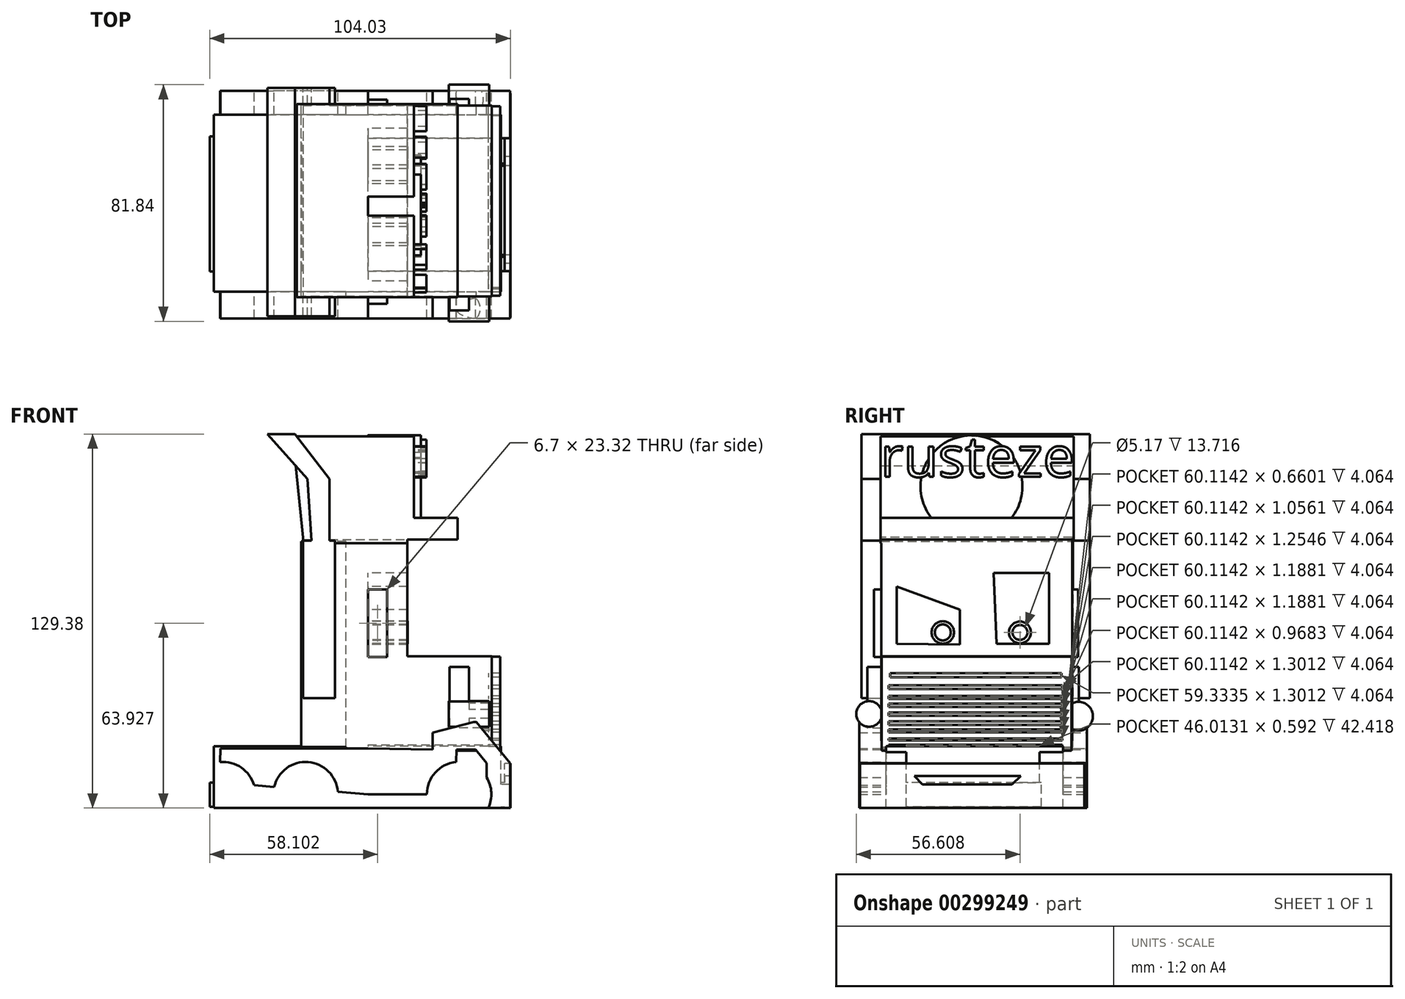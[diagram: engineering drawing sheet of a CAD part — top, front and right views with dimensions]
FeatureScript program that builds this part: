
annotation { "Feature Type Name" : "Feature", "Feature Type Description" : "" }
export const myFeature = defineFeature(function(context is Context, id is Id, definition is map)
    precondition{}
    {
        {
            var Q0;
            Q0=qCreatedBy(makeId("Front.planeOp"),FACE);
            var sketch = newSketch(context, id + "F0", { "sketchPlane" : qUnion([Q0])});
            skLineSegment(sketch, "E0", {"start": v(30.31, -25.21) * mm, "end": v(22.44, -25.21) * mm});
            skLineSegment(sketch, "E1", {"start": v(22.44, -25.21) * mm, "end": v(22.44, -3.93) * mm});
            skLineSegment(sketch, "E2", {"start": v(22.44, -3.93) * mm, "end": v(37.3, 0) * mm});
            skLineSegment(sketch, "E3", {"start": v(37.3, 0) * mm, "end": v(49.26, -14.43) * mm});
            skLineSegment(sketch, "E4", {"start": v(49.26, -14.43) * mm, "end": v(49.26, -39.2) * mm});
            skLineSegment(sketch, "E5", {"start": v(49.26, -39.2) * mm, "end": v(41.1, -34.54) * mm});
            skLineSegment(sketch, "E6", {"start": v(41.1, -34.54) * mm, "end": v(41.1, -14.43) * mm});
            skLineSegment(sketch, "E7", {"start": v(41.1, -14.43) * mm, "end": v(37.3, -9.76) * mm});
            skLineSegment(sketch, "E8", {"start": v(37.3, -9.76) * mm, "end": v(30.6, -9.76) * mm});
            skLineSegment(sketch, "E9", {"start": v(30.6, -9.76) * mm, "end": v(30.31, -25.21) * mm});
            skLineSegment(sketch, "E10", {"start": v(22.44, -9.76) * mm, "end": v(0, -9.34) * mm});
            skLineSegment(sketch, "E11", {"start": v(0, -9.34) * mm, "end": v(0, -25.21) * mm});
            skLineSegment(sketch, "E12", {"start": v(0, -25.21) * mm, "end": v(22.44, -25.21) * mm});
            skLineSegment(sketch, "E13", {"start": v(0, -9.34) * mm, "end": v(-51, -9.34) * mm});
            skLineSegment(sketch, "E14", {"start": v(-51, -9.34) * mm, "end": v(-51.23, -21.17) * mm});
            skLineSegment(sketch, "E15", {"start": v(-51.23, -21.17) * mm, "end": v(0, -25.21) * mm});
            skSolve(sketch);
        }
        {
            var Q0;
            Q0 = qSketchRegion(id + "F0", true);
            extrude(context, id + "F1", {"entities" : qUnion([Q0]), "depth" : 38.86 * mm, "hasSecondDirection" : true, "secondDirectionOppositeDirection" : true, "secondDirectionDepth" : 39.88 * mm});
        }
        {
            var Q0;
            Q0=qCreatedBy(makeId("Front.planeOp"),FACE);
            var sketch = newSketch(context, id + "F2", { "sketchPlane" : qUnion([Q0])});
            skLineSegment(sketch, "E16.bottom", {"start": v(22.74, -10.06) * mm, "end": v(42.85, -10.06) * mm});
            skLineSegment(sketch, "E16.top", {"start": v(22.74, 22.59) * mm, "end": v(42.85, 22.59) * mm});
            skLineSegment(sketch, "E16.left", {"start": v(22.74, -10.06) * mm, "end": v(22.74, 22.59) * mm});
            skLineSegment(sketch, "E16.right", {"start": v(42.85, -10.06) * mm, "end": v(42.85, 22.59) * mm});
            skLineSegment(sketch, "E17.bottom", {"start": v(22.74, -10.06) * mm, "end": v(0, -10.06) * mm});
            skLineSegment(sketch, "E17.top", {"start": v(22.74, 22.59) * mm, "end": v(0, 22.59) * mm});
            skLineSegment(sketch, "E17.right", {"start": v(0, -10.06) * mm, "end": v(0, 22.59) * mm});
            skLineSegment(sketch, "E18.bottom", {"start": v(0, -10.06) * mm, "end": v(-7.58, -10.06) * mm});
            skLineSegment(sketch, "E18.top", {"start": v(0, 22.59) * mm, "end": v(-7.58, 22.59) * mm});
            skLineSegment(sketch, "E18.right", {"start": v(-7.58, -10.06) * mm, "end": v(-7.58, 22.59) * mm});
            skLineSegment(sketch, "E19.bottom", {"start": v(-7.58, 22.59) * mm, "end": v(13.7, 22.59) * mm});
            skLineSegment(sketch, "E19.top", {"start": v(-7.58, 61.65) * mm, "end": v(13.7, 61.65) * mm});
            skLineSegment(sketch, "E19.left", {"start": v(-7.58, 22.59) * mm, "end": v(-7.58, 61.65) * mm});
            skLineSegment(sketch, "E19.right", {"start": v(13.7, 22.59) * mm, "end": v(13.7, 61.65) * mm});
            skSolve(sketch);
        }
        {
            var Q0;
            Q0 = qSketchRegion(id + "F2", true);
            extrude(context, id + "F3", {"entities" : qUnion([Q0]), "operationType" : NewBodyOperationType.ADD, "depth" : 31.24 * mm, "hasSecondDirection" : true, "secondDirectionOppositeDirection" : true, "secondDirectionDepth" : 34.8 * mm});
        }
        {
            var Q0;
            Q0=qCreatedBy(makeId("Front.planeOp"),FACE);
            var sketch = newSketch(context, id + "F4", { "sketchPlane" : qUnion([Q0])});
            skLineSegment(sketch, "E20.bottom", {"start": v(28.27, -2.77) * mm, "end": v(34.98, -2.77) * mm});
            skLineSegment(sketch, "E20.top", {"start": v(28.27, 18.8) * mm, "end": v(34.98, 18.8) * mm});
            skLineSegment(sketch, "E20.left", {"start": v(28.27, -2.77) * mm, "end": v(28.27, 18.8) * mm});
            skLineSegment(sketch, "E20.right", {"start": v(34.98, -2.77) * mm, "end": v(34.98, 18.8) * mm});
            skSolve(sketch);
        }
        {
            var Q0;
            Q0 = qSketchRegion(id + "F4", true);
            extrude(context, id + "F5", {"entities" : qUnion([Q0]), "operationType" : NewBodyOperationType.ADD, "depth" : 36.07 * mm, "hasSecondDirection" : true, "secondDirectionOppositeDirection" : true, "secondDirectionDepth" : 37.08 * mm});
        }
        {
            var Q0;
            Q0=qCreatedBy(makeId("Front.planeOp"),FACE);
            var sketch = newSketch(context, id + "F6", { "sketchPlane" : qUnion([Q0])});
            skLineSegment(sketch, "E21.bottom", {"start": v(0, 45.62) * mm, "end": v(6.7, 45.62) * mm});
            skLineSegment(sketch, "E21.top", {"start": v(0, 22.3) * mm, "end": v(6.7, 22.3) * mm});
            skLineSegment(sketch, "E21.left", {"start": v(0, 45.62) * mm, "end": v(0, 22.3) * mm});
            skLineSegment(sketch, "E21.right", {"start": v(6.7, 45.62) * mm, "end": v(6.7, 22.3) * mm});
            skSolve(sketch);
        }
        {
            var Q0;
            Q0 = qSketchRegion(id + "F6", true);
            extrude(context, id + "F7", {"entities" : qUnion([Q0]), "operationType" : NewBodyOperationType.ADD, "depth" : 33.78 * mm, "hasSecondDirection" : true, "secondDirectionOppositeDirection" : true, "secondDirectionDepth" : 36.83 * mm});
        }
        {
            var Q0;
            Q0=qCreatedBy(makeId("Front.planeOp"),FACE);
            var sketch = newSketch(context, id + "F8", { "sketchPlane" : qUnion([Q0])});
            skLineSegment(sketch, "E22.bottom", {"start": v(-7.58, -8.9) * mm, "end": v(-23.03, -8.9) * mm});
            skLineSegment(sketch, "E22.top", {"start": v(-7.58, 14.72) * mm, "end": v(-23.03, 14.72) * mm});
            skLineSegment(sketch, "E22.left", {"start": v(-7.58, -8.9) * mm, "end": v(-7.58, 14.72) * mm});
            skLineSegment(sketch, "E22.right", {"start": v(-23.03, -8.9) * mm, "end": v(-23.03, 14.72) * mm});
            skLineSegment(sketch, "E23.top", {"start": v(-7.58, 62.23) * mm, "end": v(-23.03, 62.23) * mm});
            skLineSegment(sketch, "E23.left", {"start": v(-7.58, 14.72) * mm, "end": v(-7.58, 62.23) * mm});
            skLineSegment(sketch, "E23.right", {"start": v(-23.03, 14.72) * mm, "end": v(-23.03, 62.23) * mm});
            skSolve(sketch);
        }
        {
            var Q0;
            Q0 = qSketchRegion(id + "F8", true);
            extrude(context, id + "F9", {"entities" : qUnion([Q0]), "operationType" : NewBodyOperationType.ADD, "depth" : 31.24 * mm, "hasSecondDirection" : true, "secondDirectionOppositeDirection" : true, "secondDirectionDepth" : 35.05 * mm});
        }
        {
            var Q0;
            Q0=qCreatedBy(makeId("Front.planeOp"),FACE);
            var sketch = newSketch(context, id + "F10", { "sketchPlane" : qUnion([Q0])});
            skLineSegment(sketch, "E24", {"start": v(-19.53, 8.02) * mm, "end": v(-11.37, 8.02) * mm});
            skLineSegment(sketch, "E25", {"start": v(-11.37, 8.02) * mm, "end": v(-11.37, 62.52) * mm});
            skLineSegment(sketch, "E26", {"start": v(-11.37, 62.52) * mm, "end": v(-22.44, 62.52) * mm});
            skLineSegment(sketch, "E27", {"start": v(-22.44, 62.52) * mm, "end": v(-22.44, 8.02) * mm});
            skLineSegment(sketch, "E28", {"start": v(-19.53, 8.02) * mm, "end": v(-22.44, 8.02) * mm});
            skLineSegment(sketch, "E29", {"start": v(-13.34, 62.52) * mm, "end": v(-13.34, 83.86) * mm});
            skLineSegment(sketch, "E30", {"start": v(-13.34, 83.86) * mm, "end": v(-25.2, 99.4) * mm});
            skLineSegment(sketch, "E31", {"start": v(-25.2, 99.4) * mm, "end": v(-34.7, 99.4) * mm});
            skLineSegment(sketch, "E32", {"start": v(-34.7, 99.4) * mm, "end": v(-20.93, 83.86) * mm});
            skLineSegment(sketch, "E33", {"start": v(-20.93, 83.86) * mm, "end": v(-19.53, 62.52) * mm});
            skLineSegment(sketch, "E34", {"start": v(-19.53, 62.52) * mm, "end": v(-13.34, 62.52) * mm});
            skSolve(sketch);
        }
        {
            var Q0;
            Q0 = qSketchRegion(id + "F10", true);
            extrude(context, id + "F11", {"entities" : qUnion([Q0]), "operationType" : NewBodyOperationType.ADD, "depth" : 38.1 * mm, "hasSecondDirection" : true, "secondDirectionOppositeDirection" : true, "secondDirectionDepth" : 40.9 * mm});
        }
        {
            var Q0;
            Q0=qCreatedBy(makeId("Front.planeOp"),FACE);
            var sketch = newSketch(context, id + "F12", { "sketchPlane" : qUnion([Q0])});
            skLineSegment(sketch, "E35", {"start": v(-22.36, 62.88) * mm, "end": v(31.04, 62.88) * mm});
            skLineSegment(sketch, "E36", {"start": v(31.04, 62.88) * mm, "end": v(31.04, 70.4) * mm});
            skLineSegment(sketch, "E37", {"start": v(31.04, 70.4) * mm, "end": v(15.99, 70.4) * mm});
            skLineSegment(sketch, "E38", {"start": v(15.99, 70.4) * mm, "end": v(15.99, 98.62) * mm});
            skLineSegment(sketch, "E39", {"start": v(15.99, 98.62) * mm, "end": v(-26.03, 98.62) * mm});
            skLineSegment(sketch, "E40", {"start": v(-26.03, 98.62) * mm, "end": v(-22.36, 62.88) * mm});
            skSolve(sketch);
        }
        {
            var Q0;
            Q0 = qSketchRegion(id + "F12", true);
            extrude(context, id + "F13", {"entities" : qUnion([Q0]), "operationType" : NewBodyOperationType.ADD, "depth" : 31.5 * mm, "hasSecondDirection" : true, "secondDirectionOppositeDirection" : true, "secondDirectionDepth" : 35.3 * mm});
        }
        {
            var Q0;
            Q0=qCreatedBy(makeId("Right.planeOp"),FACE);
            var sketch = newSketch(context, id + "F14", { "sketchPlane" : qUnion([Q0])});
            skLineSegment(sketch, "E41.bottom", {"start": v(23.51, -8.04) * mm, "end": v(-22.5, -8.04) * mm});
            skLineSegment(sketch, "E41.top", {"start": v(23.51, -39.28) * mm, "end": v(-22.5, -39.28) * mm});
            skLineSegment(sketch, "E41.left", {"start": v(23.51, -8.04) * mm, "end": v(23.51, -39.28) * mm});
            skLineSegment(sketch, "E41.right", {"start": v(-22.5, -8.04) * mm, "end": v(-22.5, -39.28) * mm});
            skSolve(sketch);
        }
        {
            var Q0;
            Q0 = qSketchRegion(id + "F14", true);
            extrude(context, id + "F15", {"entities" : qUnion([Q0]), "operationType" : NewBodyOperationType.REMOVE, "oppositeDirection" : true, "depth" : 104.9 * mm, "hasSecondDirection" : true, "secondDirectionOppositeDirection" : false, "secondDirectionDepth" : 66.3 * mm});
        }
        {
            var Q0;
            Q0=qCreatedBy(makeId("Front.planeOp"),FACE);
            var sketch = newSketch(context, id + "F16", { "sketchPlane" : qUnion([Q0])});
            skCircle(sketch, "E42", {"center": v(-50.09, -25.17) * mm, "radius": 11.16 * mm});
            skCircle(sketch, "E43", {"center": v(-21.54, -25.17) * mm, "radius": 11.16 * mm});
            skCircle(sketch, "E44", {"center": v(31.55, -25.17) * mm, "radius": 11.16 * mm});
            skSolve(sketch);
        }
        {
            var Q0;
            Q0 = qSketchRegion(id + "F16", true);
            extrude(context, id + "F17", {"entities" : qUnion([Q0]), "operationType" : NewBodyOperationType.REMOVE, "depth" : 52.58 * mm, "hasSecondDirection" : true, "secondDirectionOppositeDirection" : true, "secondDirectionDepth" : 51.3 * mm});
        }
        {
            var Q0;
            Q0=qCreatedBy(makeId("Front.planeOp"),FACE);
            var sketch = newSketch(context, id + "F18", { "sketchPlane" : qUnion([Q0])});
            skCircle(sketch, "E45", {"center": v(31.68, -25.5) * mm, "radius": 9.95 * mm, "construction": true});
            skCircle(sketch, "E46", {"center": v(31.68, -25.5) * mm, "radius": 3.81 * mm});
            skLineSegment(sketch, "E47", {"start": v(31.68, -25.5) * mm, "end": v(-56.9, -25.5) * mm, "construction": true});
            skCircle(sketch, "E48", {"center": v(-21.2, -25.5) * mm, "radius": 3.81 * mm});
            skCircle(sketch, "E49", {"center": v(-49.48, -25.5) * mm, "radius": 3.81 * mm});
            skSolve(sketch);
        }
        {
            var Q0;
            Q0 = qSketchRegion(id + "F18", true);
            extrude(context, id + "F19", {"entities" : qUnion([Q0]), "operationType" : NewBodyOperationType.REMOVE, "depth" : 49.02 * mm, "hasSecondDirection" : true, "secondDirectionOppositeDirection" : true, "secondDirectionDepth" : 51.56 * mm});
        }
        {
            var Q0;
            Q0 = qSketchRegion(id + "F18", true);
            extrude(context, id + "F20", {"entities" : qUnion([Q0]), "depth" : 25.4 * mm});
        }
        {
            var Q0;
            Q0=makeQuery(id+"F13.opExtrude","SWEPT_FACE",FACE,{"disambiguationData":[OSD([sQuery(id+"F12.wireOp",EDGE,"E38")])]});
            var sketch = newSketch(context, id + "F21", { "sketchPlane" : qUnion([Q0])});
            skText(sketch, "E50", { "text": "rusteze", "fontName": "OpenSans-Regular.ttf"});
            const initialGuessF21  = {"E50": [-0.0315, 0.08457, 1, 0, 0.01406]};
            skSetInitialGuess(sketch, initialGuessF21);
            skSolve(sketch);
        }
        {
            var Q0;
            Q0 = qSketchRegion(id + "F21", true);
            extrude(context, id + "F22", {"entities" : qUnion([Q0]), "operationType" : NewBodyOperationType.ADD, "depth" : 4.32 * mm});
        }
        {
            var Q0;
            Q0=qCreatedBy(makeId("Right.planeOp"),FACE);
            var sketch = newSketch(context, id + "F23", { "sketchPlane" : qUnion([Q0])});
            skCircle(sketch, "E51", {"center": v(0, 81.3) * mm, "radius": 17.63 * mm});
            skSolve(sketch);
        }
        {
            var Q0;
            Q0 = qSketchRegion(id + "F23", true);
            extrude(context, id + "F24", {"entities" : qUnion([Q0]), "operationType" : NewBodyOperationType.ADD, "depth" : 18.29 * mm});
        }
        {
            var Q0;
            Q0=qCreatedBy(makeId("Right.planeOp"),FACE);
            var sketch = newSketch(context, id + "F25", { "sketchPlane" : qUnion([Q0])});
            skLineSegment(sketch, "E52", {"start": v(-25.86, 26.89) * mm, "end": v(-25.86, 46.7) * mm});
            skLineSegment(sketch, "E53", {"start": v(-25.86, 46.7) * mm, "end": v(-4.03, 38.64) * mm});
            skLineSegment(sketch, "E54", {"start": v(-4.03, 38.64) * mm, "end": v(-4.03, 26.55) * mm});
            skLineSegment(sketch, "E55", {"start": v(-4.03, 26.55) * mm, "end": v(-25.86, 26.89) * mm});
            skLineSegment(sketch, "E56", {"start": v(7.72, 51.4) * mm, "end": v(26.87, 51.4) * mm});
            skLineSegment(sketch, "E57", {"start": v(26.87, 51.4) * mm, "end": v(26.87, 26.89) * mm});
            skLineSegment(sketch, "E58", {"start": v(26.87, 26.89) * mm, "end": v(8.73, 26.89) * mm});
            skLineSegment(sketch, "E59", {"start": v(8.73, 26.89) * mm, "end": v(7.72, 51.4) * mm});
            skSolve(sketch);
        }
        {
            var Q0;
            Q0 = qSketchRegion(id + "F25", true);
            extrude(context, id + "F26", {"entities" : qUnion([Q0]), "operationType" : NewBodyOperationType.REMOVE, "depth" : 29.72 * mm});
        }
        {
            var Q0;
            Q0=qCreatedBy(makeId("Right.planeOp"),FACE);
            var sketch = newSketch(context, id + "F27", { "sketchPlane" : qUnion([Q0])});
            skCircle(sketch, "E60", {"center": v(-9.9, 30.78) * mm, "radius": 3.88 * mm});
            skCircle(sketch, "E61", {"center": v(-9.9, 30.78) * mm, "radius": 2.77 * mm});
            skCircle(sketch, "E62", {"center": v(16.78, 30.78) * mm, "radius": 3.8 * mm});
            skCircle(sketch, "E63", {"center": v(16.78, 30.78) * mm, "radius": 2.58 * mm});
            skSolve(sketch);
        }
        {
            var Q0;
            Q0 = qSketchRegion(id + "F27", true);
            extrude(context, id + "F28", {"entities" : qUnion([Q0]), "operationType" : NewBodyOperationType.ADD, "depth" : 13.72 * mm});
        }
        {
            var Q0;
            Q0=qCreatedBy(makeId("Right.planeOp"),FACE);
            var sketch = newSketch(context, id + "F29", { "sketchPlane" : qUnion([Q0])});
            skCircle(sketch, "E64", {"center": v(-35.4, 2.58) * mm, "radius": 4.44 * mm});
            skCircle(sketch, "E65", {"center": v(37.02, 1.8) * mm, "radius": 4.99 * mm});
            skSolve(sketch);
        }
        {
            var Q0;
            Q0 = qSketchRegion(id + "F29", true);
            extrude(context, id + "F30", {"entities" : qUnion([Q0]), "operationType" : NewBodyOperationType.ADD, "depth" : 41.9 * mm, "hasSecondDirection" : true, "secondDirectionOppositeDirection" : false, "secondDirectionDepth" : 27.94 * mm});
        }
        {
            var Q0;
            Q0=qCreatedBy(makeId("Right.planeOp"),FACE);
            var sketch = newSketch(context, id + "F31", { "sketchPlane" : qUnion([Q0])});
            skLineSegment(sketch, "E66.bottom", {"start": v(-31.02, 22.35) * mm, "end": v(34.56, 22.35) * mm});
            skLineSegment(sketch, "E66.top", {"start": v(-31.02, -21.63) * mm, "end": v(34.56, -21.63) * mm});
            skLineSegment(sketch, "E66.left", {"start": v(-31.02, 22.35) * mm, "end": v(-31.02, -21.63) * mm});
            skLineSegment(sketch, "E66.right", {"start": v(34.56, 22.35) * mm, "end": v(34.56, -21.63) * mm});
            skSolve(sketch);
        }
        {
            var Q0;
            Q0 = qSketchRegion(id + "F31", true);
            extrude(context, id + "F32", {"entities" : qUnion([Q0]), "operationType" : NewBodyOperationType.ADD, "depth" : 45.72 * mm, "hasSecondDirection" : true, "secondDirectionOppositeDirection" : false, "secondDirectionDepth" : 42.42 * mm});
        }
        {
            var Q0;
            Q0=makeQuery(id+"F32.opExtrude","CAP_FACE",FACE,{"disambiguationData":[OSD([sQuery(id+"F31.wireOp",EDGE,"E66.bottom"),sQuery(id+"F31.wireOp",EDGE,"E66.top"),sQuery(id+"F31.wireOp",EDGE,"E66.left"),sQuery(id+"F31.wireOp",EDGE,"E66.right")])],"isStart":false});
            var sketch = newSketch(context, id + "F33", { "sketchPlane" : qUnion([Q0])});
            skLineSegment(sketch, "E67.bottom", {"start": v(-28.16, 16.63) * mm, "end": v(31.18, 16.63) * mm});
            skLineSegment(sketch, "E67.top", {"start": v(-28.16, 15.33) * mm, "end": v(31.18, 15.33) * mm});
            skLineSegment(sketch, "E67.left", {"start": v(-28.16, 16.63) * mm, "end": v(-28.16, 15.33) * mm});
            skLineSegment(sketch, "E67.right", {"start": v(31.18, 16.63) * mm, "end": v(31.18, 15.33) * mm});
            skLineSegment(sketch, "E68.bottom", {"start": v(-28.68, 12.47) * mm, "end": v(31.44, 12.47) * mm});
            skLineSegment(sketch, "E68.top", {"start": v(-28.68, 11.16) * mm, "end": v(31.44, 11.16) * mm});
            skLineSegment(sketch, "E68.left", {"start": v(-28.68, 12.47) * mm, "end": v(-28.68, 11.16) * mm});
            skLineSegment(sketch, "E68.right", {"start": v(31.44, 12.47) * mm, "end": v(31.44, 11.16) * mm});
            skLineSegment(sketch, "E69.bottom", {"start": v(-28.68, 8.82) * mm, "end": v(31.44, 8.82) * mm});
            skLineSegment(sketch, "E69.top", {"start": v(-28.68, 7.85) * mm, "end": v(31.44, 7.85) * mm});
            skLineSegment(sketch, "E69.left", {"start": v(-28.68, 8.82) * mm, "end": v(-28.68, 7.85) * mm});
            skLineSegment(sketch, "E69.right", {"start": v(31.44, 8.82) * mm, "end": v(31.44, 7.85) * mm});
            skLineSegment(sketch, "E70.bottom", {"start": v(-28.68, 6.14) * mm, "end": v(31.44, 6.14) * mm});
            skLineSegment(sketch, "E70.top", {"start": v(-28.68, 4.95) * mm, "end": v(31.44, 4.95) * mm});
            skLineSegment(sketch, "E70.left", {"start": v(-28.68, 6.14) * mm, "end": v(-28.68, 4.95) * mm});
            skLineSegment(sketch, "E70.right", {"start": v(31.44, 6.14) * mm, "end": v(31.44, 4.95) * mm});
            skLineSegment(sketch, "E71.bottom", {"start": v(-28.68, 3.1) * mm, "end": v(31.44, 3.1) * mm});
            skLineSegment(sketch, "E71.top", {"start": v(-28.68, 1.91) * mm, "end": v(31.44, 1.91) * mm});
            skLineSegment(sketch, "E71.left", {"start": v(-28.68, 3.1) * mm, "end": v(-28.68, 1.91) * mm});
            skLineSegment(sketch, "E71.right", {"start": v(31.44, 3.1) * mm, "end": v(31.44, 1.91) * mm});
            skLineSegment(sketch, "E72.bottom", {"start": v(-28.68, 0) * mm, "end": v(31.44, 0) * mm});
            skLineSegment(sketch, "E72.top", {"start": v(-28.68, -1.25) * mm, "end": v(31.44, -1.25) * mm});
            skLineSegment(sketch, "E72.left", {"start": v(-28.68, 0) * mm, "end": v(-28.68, -1.25) * mm});
            skLineSegment(sketch, "E72.right", {"start": v(31.44, 0) * mm, "end": v(31.44, -1.25) * mm});
            skLineSegment(sketch, "E73.bottom", {"start": v(-28.68, -2.7) * mm, "end": v(31.44, -2.7) * mm});
            skLineSegment(sketch, "E73.top", {"start": v(-28.68, -3.76) * mm, "end": v(31.44, -3.76) * mm});
            skLineSegment(sketch, "E73.left", {"start": v(-28.68, -2.7) * mm, "end": v(-28.68, -3.76) * mm});
            skLineSegment(sketch, "E73.right", {"start": v(31.44, -2.7) * mm, "end": v(31.44, -3.76) * mm});
            skLineSegment(sketch, "E74.bottom", {"start": v(-28.68, -5.87) * mm, "end": v(31.44, -5.87) * mm});
            skLineSegment(sketch, "E74.top", {"start": v(-28.68, -6.53) * mm, "end": v(31.44, -6.53) * mm});
            skLineSegment(sketch, "E74.left", {"start": v(-28.68, -5.87) * mm, "end": v(-28.68, -6.53) * mm});
            skLineSegment(sketch, "E74.right", {"start": v(31.44, -5.87) * mm, "end": v(31.44, -6.53) * mm});
            skLineSegment(sketch, "E75.bottom", {"start": v(-28.68, -8.12) * mm, "end": v(31.44, -8.12) * mm});
            skLineSegment(sketch, "E75.top", {"start": v(-28.68, -8.88) * mm, "end": v(31.44, -8.88) * mm});
            skLineSegment(sketch, "E75.left", {"start": v(-28.68, -8.12) * mm, "end": v(-28.68, -8.88) * mm});
            skLineSegment(sketch, "E75.right", {"start": v(31.44, -8.12) * mm, "end": v(31.44, -8.88) * mm});
            skSolve(sketch);
        }
        {
            var Q0;
            Q0 = qSketchRegion(id + "F33", true);
            extrude(context, id + "F34", {"entities" : qUnion([Q0]), "operationType" : NewBodyOperationType.REMOVE, "depth" : 11.18 * mm, "hasSecondDirection" : true, "secondDirectionOppositeDirection" : true, "secondDirectionDepth" : 4.06 * mm});
        }
        {
            var Q0;
            Q0 = qSketchRegion(id + "F33", true);
            extrude(context, id + "F35", {"entities" : qUnion([Q0]), "operationType" : NewBodyOperationType.REMOVE, "depth" : 14.48 * mm});
        }
        {
            var Q0;
            Q0=qCreatedBy(makeId("Right.planeOp"),FACE);
            var sketch = newSketch(context, id + "F36", { "sketchPlane" : qUnion([Q0])});
            skLineSegment(sketch, "E76.bottom", {"start": v(-38.55, -14.5) * mm, "end": v(38.98, -14.5) * mm});
            skLineSegment(sketch, "E76.top", {"start": v(-38.55, -38.83) * mm, "end": v(38.98, -38.83) * mm});
            skLineSegment(sketch, "E76.left", {"start": v(-38.55, -14.5) * mm, "end": v(-38.55, -38.83) * mm});
            skLineSegment(sketch, "E76.right", {"start": v(38.98, -14.5) * mm, "end": v(38.98, -38.83) * mm});
            skSolve(sketch);
        }
        {
            var Q0;
            Q0 = qSketchRegion(id + "F36", true);
            extrude(context, id + "F37", {"entities" : qUnion([Q0]), "operationType" : NewBodyOperationType.ADD, "depth" : 49.28 * mm, "hasSecondDirection" : true, "secondDirectionOppositeDirection" : false, "secondDirectionDepth" : 47.24 * mm});
        }
        {
            var Q0;
            Q0=qCreatedBy(makeId("Front.planeOp"),FACE);
            var sketch = newSketch(context, id + "F38", { "sketchPlane" : qUnion([Q0])});
            skLineSegment(sketch, "E77.bottom", {"start": v(50.04, -29.88) * mm, "end": v(40.98, -29.88) * mm});
            skLineSegment(sketch, "E77.top", {"start": v(50.04, -44.32) * mm, "end": v(40.98, -44.32) * mm});
            skLineSegment(sketch, "E77.left", {"start": v(50.04, -29.88) * mm, "end": v(50.04, -44.32) * mm});
            skLineSegment(sketch, "E77.right", {"start": v(40.98, -29.88) * mm, "end": v(40.98, -44.32) * mm});
            skSolve(sketch);
        }
        {
            var Q0;
            Q0 = qSketchRegion(id + "F38", true);
            extrude(context, id + "F39", {"entities" : qUnion([Q0]), "operationType" : NewBodyOperationType.REMOVE, "oppositeDirection" : true, "depth" : 40.9 * mm, "hasSecondDirection" : true, "secondDirectionOppositeDirection" : false, "secondDirectionDepth" : 39.37 * mm});
        }
        {
            var Q0;
            Q0=qCreatedBy(makeId("Front.planeOp"),FACE);
            var sketch = newSketch(context, id + "F40", { "sketchPlane" : qUnion([Q0])});
            skLineSegment(sketch, "E78.bottom", {"start": v(49.04, -29.54) * mm, "end": v(-54.75, -29.54) * mm});
            skLineSegment(sketch, "E78.top", {"start": v(49.04, -21.14) * mm, "end": v(-54.75, -21.14) * mm});
            skLineSegment(sketch, "E78.left", {"start": v(49.04, -29.54) * mm, "end": v(49.04, -21.14) * mm});
            skLineSegment(sketch, "E78.right", {"start": v(-54.75, -29.54) * mm, "end": v(-54.75, -21.14) * mm});
            skSolve(sketch);
        }
        {
            var Q0;
            Q0 = qSketchRegion(id + "F40", true);
            extrude(context, id + "F41", {"entities" : qUnion([Q0]), "operationType" : NewBodyOperationType.ADD, "depth" : 22.6 * mm, "hasSecondDirection" : true, "secondDirectionOppositeDirection" : true, "secondDirectionDepth" : 24.13 * mm});
        }
        {
            var Q0;
            {var subQ0=sQuery(id+"F2.wireOp",EDGE,"E16.right");var subQ1=sQuery(id+"F2.wireOp",EDGE,"E17.top");var subQ2=sQuery(id+"F2.wireOp",EDGE,"E16.top");var subQ3=sQuery(id+"F2.wireOp",EDGE,"E19.left");var subQ4=sQuery(id+"F2.wireOp",EDGE,"E18.right");var subQ5=sQuery(id+"F2.wireOp",EDGE,"E19.top");var subQ6=sQuery(id+"F2.wireOp",EDGE,"E19.right");Q0=makeQuery(id+"F9.boolean.opBoolean","MERGE",FACE,{"derivedFrom":[makeQuery(id+"F3.boolean.opBoolean","SPLIT",FACE,{"disambiguationData":[TD([makeQuery(id+"F1.opExtrude","SWEPT_FACE",FACE,{"disambiguationData":[OSD([sQuery(id+"F0.wireOp",EDGE,"E1")])]})])],"derivedFrom":makeQuery(id+"F3.opExtrude","CAP_FACE",FACE,{"disambiguationData":[OSD([sQuery(id+"F2.wireOp",EDGE,"E16.bottom"),subQ2,subQ0,sQuery(id+"F2.wireOp",EDGE,"E17.bottom"),subQ1,sQuery(id+"F2.wireOp",EDGE,"E18.bottom"),subQ4,subQ5,subQ3,subQ6])],"isStart":false})}),makeQuery(id+"F9.opExtrude","CAP_FACE",FACE,{"disambiguationData":[OSD([sQuery(id+"F8.wireOp",EDGE,"E22.bottom"),sQuery(id+"F8.wireOp",EDGE,"E22.left"),sQuery(id+"F8.wireOp",EDGE,"E22.right"),sQuery(id+"F8.wireOp",EDGE,"E23.top"),sQuery(id+"F8.wireOp",EDGE,"E23.left"),sQuery(id+"F8.wireOp",EDGE,"E23.right")])],"isStart":false})]});}
            var sketch = newSketch(context, id + "F42", { "sketchPlane" : qUnion([Q0])});
            skLineSegment(sketch, "E79.bottom", {"start": v(13.7, 61.65) * mm, "end": v(-22.44, 61.65) * mm});
            skLineSegment(sketch, "E79.top", {"start": v(13.7, 66.18) * mm, "end": v(-22.44, 66.18) * mm});
            skLineSegment(sketch, "E79.left", {"start": v(13.7, 61.65) * mm, "end": v(13.7, 66.18) * mm});
            skLineSegment(sketch, "E79.right", {"start": v(-22.44, 61.65) * mm, "end": v(-22.44, 66.18) * mm});
            skSolve(sketch);
        }
        {
            var Q0;
            Q0 = qSketchRegion(id + "F42", true);
            extrude(context, id + "F43", {"entities" : qUnion([Q0]), "operationType" : NewBodyOperationType.ADD, "depth" : 0.25 * mm, "hasSecondDirection" : true, "secondDirectionOppositeDirection" : true, "secondDirectionDepth" : 66.04 * mm});
        }
        {
            var Q0;
            Q0=qCreatedBy(makeId("Top.planeOp"),FACE);
            var sketch = newSketch(context, id + "F44", { "sketchPlane" : qUnion([Q0])});
            skCircle(sketch, "E80", {"center": v(-49.68, -44.16) * mm, "radius": 1.27 * mm});
            skLineSegment(sketch, "E81", {"start": v(-53.27, -49.24) * mm, "end": v(35.41, -49.24) * mm, "construction": true});
            skCircle(sketch, "E82", {"center": v(-21.7, -44.16) * mm, "radius": 1.27 * mm});
            skCircle(sketch, "E83", {"center": v(32.06, -44.16) * mm, "radius": 1.27 * mm});
            skCircle(sketch, "E84", {"center": v(-49.32, 46.09) * mm, "radius": 1.27 * mm});
            skCircle(sketch, "E85", {"center": v(-20.9, 46.09) * mm, "radius": 1.27 * mm});
            skCircle(sketch, "E86", {"center": v(32, 46.09) * mm, "radius": 1.27 * mm});
            skLineSegment(sketch, "E87", {"start": v(-53.28, 51.17) * mm, "end": v(35.96, 51.17) * mm, "construction": true});
            skSolve(sketch);
        }
        {
            var Q0;
            Q0 = qSketchRegion(id + "F44", true);
            extrude(context, id + "F45", {"entities" : qUnion([Q0]), "operationType" : NewBodyOperationType.REMOVE, "oppositeDirection" : true, "depth" : 41.9 * mm});
        }
        {
            var Q0;
            Q0=qCreatedBy(makeId("Right.planeOp"),FACE);
            var sketch = newSketch(context, id + "F46", { "sketchPlane" : qUnion([Q0])});
            skLineSegment(sketch, "E88", {"start": v(-19.8, -18.92) * mm, "end": v(17.08, -18.92) * mm});
            skLineSegment(sketch, "E89", {"start": v(17.08, -18.92) * mm, "end": v(14, -21.8) * mm});
            skLineSegment(sketch, "E90", {"start": v(14, -21.8) * mm, "end": v(-16.92, -21.8) * mm});
            skLineSegment(sketch, "E91", {"start": v(-16.92, -21.8) * mm, "end": v(-19.8, -18.92) * mm});
            skSolve(sketch);
        }
        {
            var Q0;
            Q0 = qSketchRegion(id + "F46", true);
            extrude(context, id + "F47", {"entities" : qUnion([Q0]), "operationType" : NewBodyOperationType.REMOVE, "depth" : 66.04 * mm, "hasSecondDirection" : true, "secondDirectionOppositeDirection" : false, "secondDirectionDepth" : 44.7 * mm});
        }
        {
            var Q0;
            Q0=qCreatedBy(makeId("Right.planeOp"),FACE);
            var sketch = newSketch(context, id + "F48", { "sketchPlane" : qUnion([Q0])});
            skLineSegment(sketch, "E92.bottom", {"start": v(23.85, 0) * mm, "end": v(-22.5, 0) * mm});
            skLineSegment(sketch, "E92.top", {"start": v(23.85, -29.54) * mm, "end": v(-22.5, -29.54) * mm});
            skLineSegment(sketch, "E92.left", {"start": v(23.85, 0) * mm, "end": v(23.85, -29.54) * mm});
            skLineSegment(sketch, "E92.right", {"start": v(-22.5, 0) * mm, "end": v(-22.5, -29.54) * mm});
            skSolve(sketch);
        }
        {
            var Q0;
            Q0 = qSketchRegion(id + "F48", true);
            extrude(context, id + "F49", {"entities" : qUnion([Q0]), "operationType" : NewBodyOperationType.ADD, "oppositeDirection" : true, "depth" : 22.86 * mm});
        }
        {
            var Q0;
            Q0=qCreatedBy(makeId("Top.planeOp"),FACE);
            var sketch = newSketch(context, id + "F50", { "sketchPlane" : qUnion([Q0])});
            skLineSegment(sketch, "E93.bottom", {"start": v(-53.34, -29.58) * mm, "end": v(46.05, -29.58) * mm});
            skLineSegment(sketch, "E93.top", {"start": v(-53.34, 31.63) * mm, "end": v(46.05, 31.63) * mm});
            skLineSegment(sketch, "E93.left", {"start": v(-53.34, -29.58) * mm, "end": v(-53.34, 31.63) * mm});
            skLineSegment(sketch, "E93.right", {"start": v(46.05, -29.58) * mm, "end": v(46.05, 31.63) * mm});
            skSolve(sketch);
        }
        {
            var Q0;
            Q0 = qSketchRegion(id + "F50", true);
            extrude(context, id + "F51", {"entities" : qUnion([Q0]), "operationType" : NewBodyOperationType.ADD, "oppositeDirection" : true, "depth" : 29.97 * mm, "hasSecondDirection" : true, "secondDirectionOppositeDirection" : true, "secondDirectionDepth" : 8.64 * mm});
        }
    });
